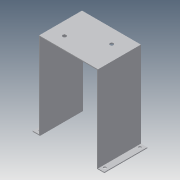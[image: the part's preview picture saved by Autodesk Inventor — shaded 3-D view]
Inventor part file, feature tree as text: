
AUTODESK INVENTOR PART (.ipt)
format: ipt  version: 2014 (Build 180170000, 170)  size: 111,616 bytes
history: native  units: in
note: dims shown in document units (in); Inventor stores cm internally (conversion verified against a paired STEP export)
features: sketch x3, extrude x2, hole x1, projected_geometry x1
ambient origin geometry x8: Origin, YZ Plane, XZ Plane, XY Plane, X Axis, Y Axis, Z Axis, Center Point
bodies: Solid1 (feature_tree)
feature tree (7):
  extrude  "Extrusion1"  Depth=4.0in
  hole  "Hole1"  [1 undecoded]
  extrude  "Extrusion2"  Depth=3.0in TaperAngle=0.0deg
  sketch  "Sketch1"  dims[d0=6.0in d1=4.0in]
  sketch  "Sketch2"  dims[d3=0.5in d4=0.5in]
  projected_geometry  "Projected Loop1"
  sketch  "Sketch3"  dims[d5=0.06in d6=3.0in d7=0.0in d8=0.19in d9=0.75in d10=0.375in d11=0.25in d12=0.5635in d13=1.0in d14=0.8108in d15=2.9in d16=1.9in d17=0.1875in d18=0.25in d19=0.25in d20=0.375in d21=0.375in d22=0.375in d23=0.375in d24=3.0in d25=0.0in]
note: 1 required parameter value undecoded (feature->parameter linkage not recoverable at this tier; creation-order binding heuristic only, values carry confidence <= 0.55)
